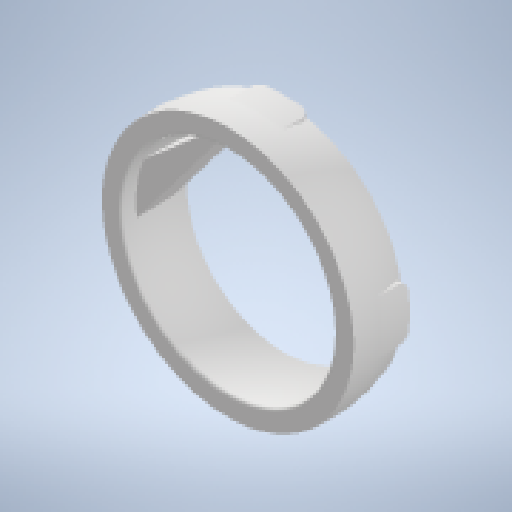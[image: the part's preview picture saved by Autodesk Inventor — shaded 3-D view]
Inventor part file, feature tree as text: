
AUTODESK INVENTOR PART (.ipt)
format: ipt  version: 2025.1 (Build 291241000, 241)  size: 302,080 bytes
history: native  units: mm
features: sketch x9, extrude x7, chamfer x5, fillet x5, revolve x2, plane x1
ambient origin geometry x8: Origin, YZ Plane, XZ Plane, XY Plane, X Axis, Y Axis, Z Axis, Center Point
bodies: Volumenkörper1 (feature_tree)
feature tree (29):
  revolve  "Umdrehung1"
  revolve  "Umdrehung2"
  extrude  "Extrusion1"  Depth=9.0mm
  plane  "Arbeitsebene3"
  extrude  "Extrusion2"  Depth=9.0mm
  extrude  "Extrusion3"  TaperAngle=0.0deg  [1 undecoded]
  extrude  "Extrusion4"  Depth=7.575mm
  extrude  "Extrusion5"  Depth=7.575mm
  extrude  "Extrusion6"  Depth=4.0mm
  extrude  "Extrusion7"  Depth=30.0mm TaperAngle=0.0deg
  chamfer  "Fasen1"  Distance=3.0mm
  chamfer  "Fasen2"  Distance=15.2mm
  chamfer  "Fasen3"  Distance=14.2mm
  chamfer  "Fasen4"  Distance=1.8mm
  chamfer  "Fasen5"  Distance=0.6mm
  fillet  "Rundung2"  Radius=1.8mm
  fillet  "Rundung3"  Radius=0.6mm
  fillet  "Rundung4"  Radius=1.8mm
  fillet  "Rundung5"  Radius=0.6mm
  fillet  "Rundung6"  Radius=1.8mm
  sketch  "Skizze2"  dims[d2=9.0mm d3=18.0mm]
  sketch  "Skizze3"  dims[d4=9.0mm d5=9.0mm]
  sketch  "Skizze4"  dims[d6=90.0deg d7=0.0mm]
  sketch  "Skizze5"  dims[d8=7.575mm d9=15.15mm]
  sketch  "Skizze6"  dims[d10=7.575mm d11=7.575mm]
  sketch  "Skizze7"  dims[d12=90.0deg d13=4.0mm]
  sketch  "Skizze8"  dims[d14=1.0mm d15=30.0mm d16=0.0mm]
  sketch  "Skizze9"  dims[d17=15.0mm]
  sketch  "Skizze11"  dims[d18=15.0mm d19=3.0mm d22=15.2mm d23=0.0mm d28=14.2mm d29=0.0mm d30=1.8mm d31=0.6mm d32=0.0mm d33=1.8mm d34=0.6mm d35=0.0mm d36=1.8mm d37=0.6mm d38=0.0mm d39=1.8mm d40=0.6mm d41=0.0mm d42=2.0mm d43=2.0mm d44=45.0deg d45=0.7mm d46=2.0mm d47=45.0deg d48=0.7mm d49=2.0mm d50=45.0deg d51=1.5mm d52=2.0mm d53=45.0deg d54=1.5mm d55=2.0mm d56=45.0deg d58=0.8mm d59=0.8mm d60=0.4mm d61=0.2mm d62=0.2mm d66=3.8mm d67=11.6mm]
note: 1 required parameter value undecoded (feature->parameter linkage not recoverable at this tier; creation-order binding heuristic only, values carry confidence <= 0.55)
